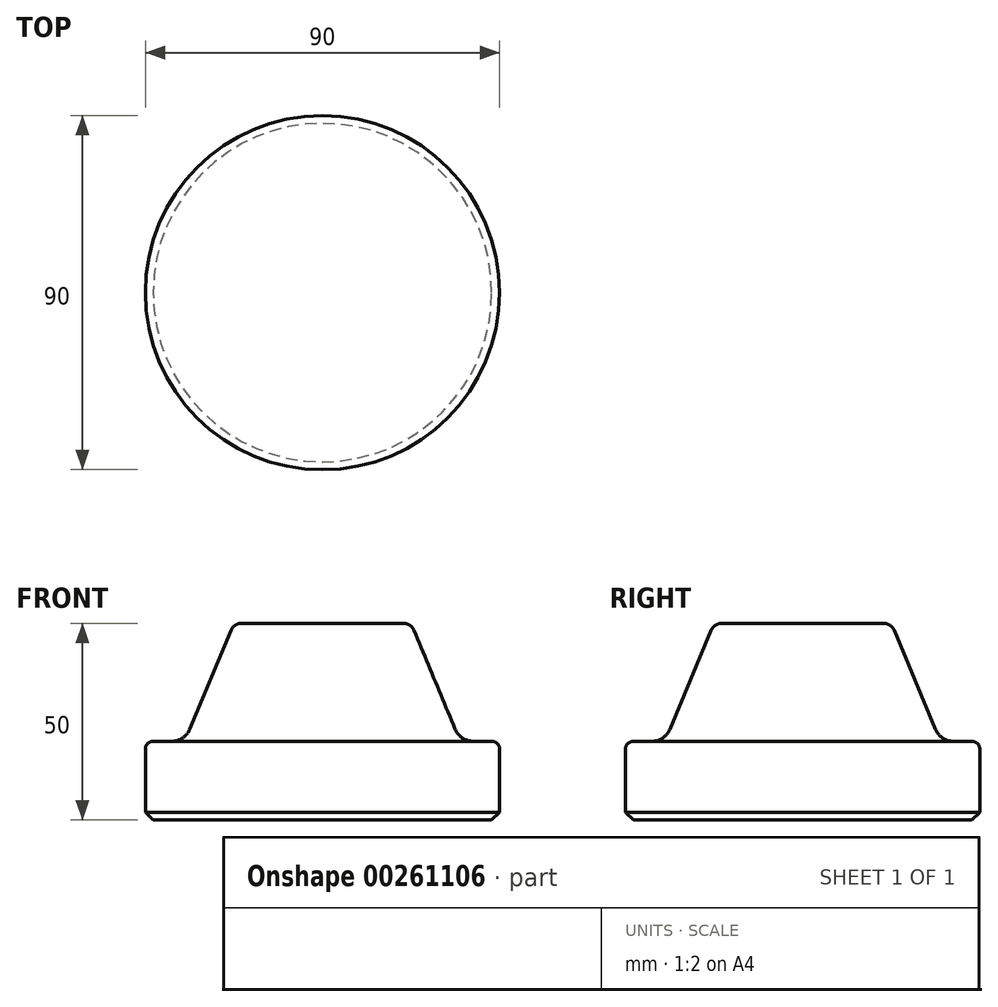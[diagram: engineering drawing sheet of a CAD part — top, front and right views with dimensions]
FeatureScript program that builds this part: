
annotation { "Feature Type Name" : "Feature", "Feature Type Description" : "" }
export const myFeature = defineFeature(function(context is Context, id is Id, definition is map)
    precondition{}
    {
        {
            var Q0;
            Q0=qCreatedBy(makeId("Front.planeOp"),FACE);
            var sketch = newSketch(context, id + "F0", { "sketchPlane" : qUnion([Q0])});
            skLineSegment(sketch, "E0", {"start": v(0, 0) * mm, "end": v(0, 50) * mm});
            skLineSegment(sketch, "E1", {"start": v(0, 50) * mm, "end": v(20.5, 50) * mm});
            skLineSegment(sketch, "E2", {"start": v(23.27, 48.15) * mm, "end": v(33.72, 23.08) * mm});
            skLineSegment(sketch, "E3", {"start": v(38.33, 20) * mm, "end": v(43, 20) * mm});
            skLineSegment(sketch, "E4", {"start": v(45, 18) * mm, "end": v(45, 0) * mm});
            skLineSegment(sketch, "E5", {"start": v(45, 0) * mm, "end": v(0, 0) * mm});
            skPoint(sketch, "E6.visualSharp", {"position": v(22.5, 50) * mm});
            skArc(sketch, "E6.filletArc", {"start": v(23.27, 48.15) * mm, "mid": v(22.16, 49.5) * mm, "end": v(20.5, 50) * mm});
            skPoint(sketch, "E7.visualSharp", {"position": v(35, 20) * mm});
            skArc(sketch, "E7.filletArc", {"start": v(33.72, 23.08) * mm, "mid": v(35.56, 20.84) * mm, "end": v(38.33, 20) * mm});
            skPoint(sketch, "E8.visualSharp", {"position": v(45, 20) * mm});
            skArc(sketch, "E8.filletArc", {"start": v(45, 18) * mm, "mid": v(44.41, 19.41) * mm, "end": v(43, 20) * mm});
            skLineSegment(sketch, "E9", {"start": v(0, -34.66) * mm, "end": v(0, -31.2) * mm});
            skLineSegment(sketch, "E10", {"start": v(0, 63.08) * mm, "end": v(0, -24.04) * mm, "construction": true});
            skSolve(sketch);
        }
        {
            var Q0;
            Q0 = qSketchRegion(id + "F0", true);
            var Q1;
            Q1=sQuery(id+"F0.wireOp",EDGE,"E10");
            revolve(context, id + "F1", {"entities" : qUnion([Q0]), "axis" : qUnion([Q1]), "revolveType" : RevolveType.FULL});
        }
        {
            var Q0;
            Q0=makeQuery(id+"F1.opRevolve","SWEPT_FACE",FACE,{"disambiguationData":[OSD([sQuery(id+"F0.wireOp",EDGE,"E5")])]});
            chamfer(context, id + "F2", {"entities" : qUnion([Q0]), "width" : 2 * mm, "tangentPropagation" : true});
        }
    });
